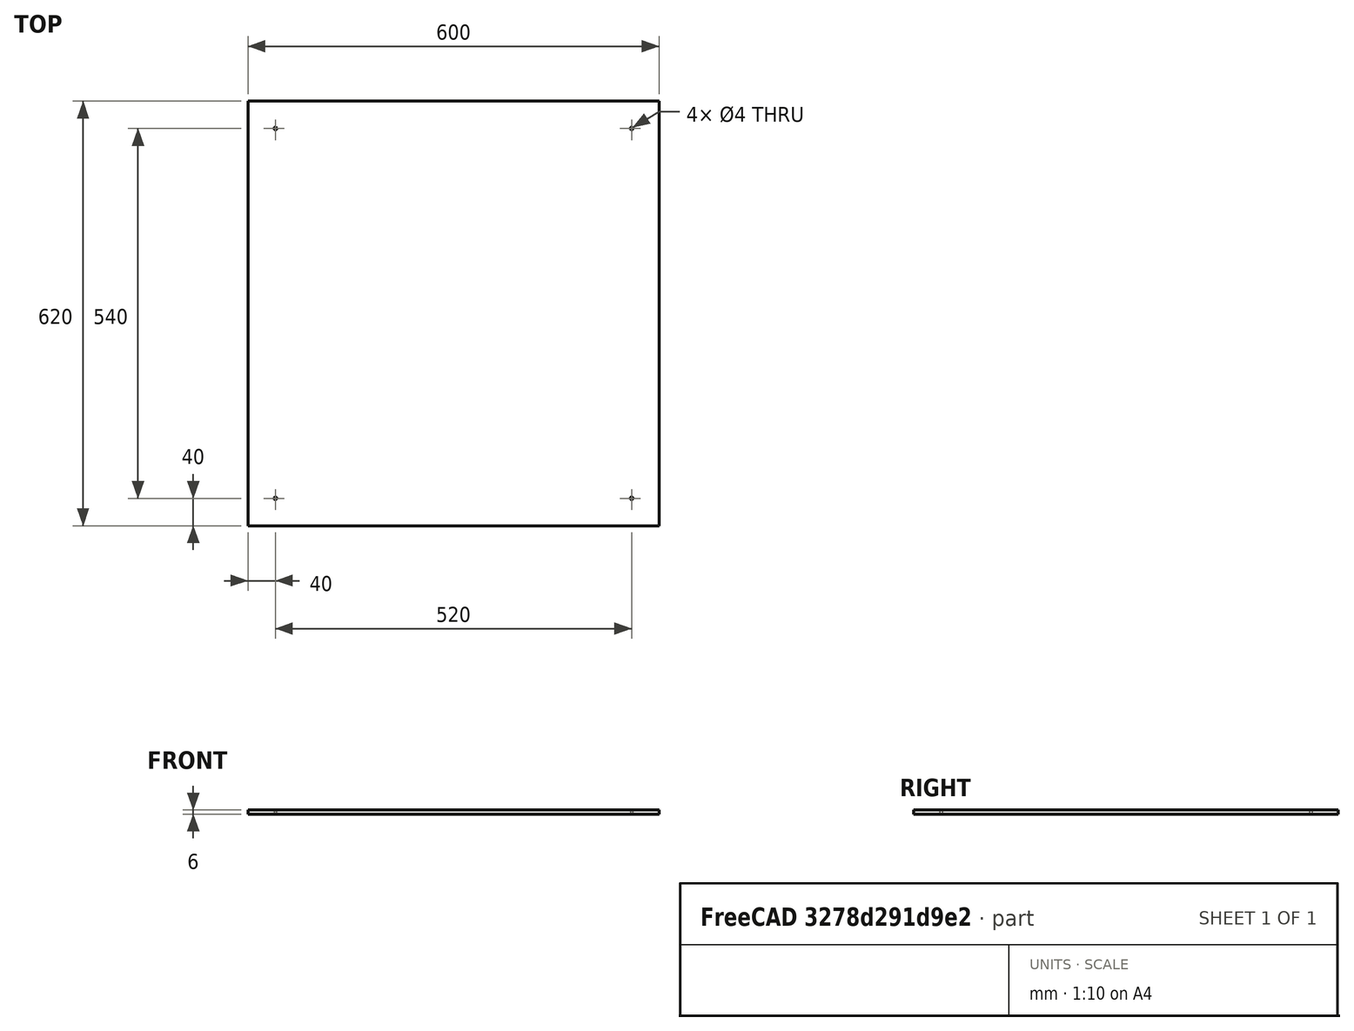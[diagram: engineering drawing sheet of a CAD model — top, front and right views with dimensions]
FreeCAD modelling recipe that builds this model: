
FCSTD DOCUMENT  (FreeCAD 1.0R39319 (Git))
Label: glass
License: All rights reserved
LicenseURL: https://en.wikipedia.org/wiki/All_rights_reserved
objects: Sketcher::SketchObject×1, PartDesign::Pad×1, PartDesign::Body×1
note: 6 computed .brp shape members not serialized (recipe doc carries the construction recipe); baked Part::Feature solids carry a one-line shape summary decoded from their .brp

FEATURE [Sketcher::SketchObject] Sketch  label="glass_s"
  ArcFitTolerance = 1e-06
  AttachmentSupport = -> [XY_Plane]
  FullyConstrained = true
  MakeInternals = false
  MapMode = 5
  sketch-geometry (16):
    g0: LineSegment StartX=0 StartY=0 StartZ=0 EndX=600 EndY=0 EndZ=0
    g1: LineSegment StartX=600 StartY=0 StartZ=0 EndX=600 EndY=620 EndZ=0
    g2: LineSegment StartX=600 StartY=620 StartZ=0 EndX=0 EndY=620 EndZ=0
    g3: LineSegment StartX=0 StartY=620 StartZ=0 EndX=0 EndY=0 EndZ=0
    g4: Circle CenterX=40 CenterY=580 CenterZ=0 NormalX=0 NormalY=0 NormalZ=1 AngleXU=0 Radius=2
    g5: Circle CenterX=560 CenterY=580 CenterZ=0 NormalX=0 NormalY=0 NormalZ=1 AngleXU=0 Radius=2
    g6: Circle CenterX=560 CenterY=40 CenterZ=0 NormalX=0 NormalY=0 NormalZ=1 AngleXU=0 Radius=2
    g7: Circle CenterX=40 CenterY=40 CenterZ=0 NormalX=0 NormalY=0 NormalZ=1 AngleXU=0 Radius=2
    g8: LineSegment [constr] StartX=40 StartY=580 StartZ=0 EndX=40 EndY=40 EndZ=0
    g9: LineSegment [constr] StartX=40 StartY=40 StartZ=0 EndX=560 EndY=40 EndZ=0
    g10: LineSegment [constr] StartX=560 StartY=40 StartZ=0 EndX=560 EndY=580 EndZ=0
    g11: LineSegment [constr] StartX=560 StartY=580 StartZ=0 EndX=40 EndY=580 EndZ=0
    g12: LineSegment [constr] StartX=560 StartY=580 StartZ=0 EndX=560 EndY=620 EndZ=0
    g13: LineSegment [constr] StartX=560 StartY=580 StartZ=0 EndX=600 EndY=580 EndZ=0
    g14: LineSegment [constr] StartX=40 StartY=40 StartZ=0 EndX=40 EndY=0 EndZ=0
    g15: LineSegment [constr] StartX=40 StartY=40 StartZ=0 EndX=0 EndY=40 EndZ=0
  constraints (43):
    c: Coincident(g0,g1)
    c: Coincident(g1,g2)
    c: Coincident(g2,g3)
    c: Coincident(g3,g0)
    c: Horizontal(g0)
    c: Horizontal(g2)
    c: Vertical(g1)
    c: Vertical(g3)
    c: Coincident(g0,g-1)
    c: DistanceY(g3,g3) = 620
    c: DistanceX(g2,g2) = 600
    c: Coincident(g8,g9)
    c: Coincident(g9,g10)
    c: Coincident(g10,g11)
    c: Coincident(g11,g8)
    c: Vertical(g8)
    c: Vertical(g10)
    c: Horizontal(g9)
    c: Horizontal(g11)
    c: Coincident(g8,g4)
    c: Coincident(g9,g6)
    c: Coincident(g7,g8)
    c: Coincident(g10,g5)
    c: Diameter(g4) = 4
    c: Equal(g4,g7)
    c: Equal(g7,g6)
    c: Equal(g6,g5)
    c: DistanceX(g0,g7) = 40
    c: Coincident(g12,g5)
    c: PointOnObject(g12,g2)
    c: Vertical(g12)
    c: PointOnObject(g13,g1)
    c: Horizontal(g13)
    c: Coincident(g13,g5)
    c: Coincident(g14,g7)
    c: PointOnObject(g14,g0)
    c: Vertical(g14)
    c: Coincident(g15,g7)
    c: PointOnObject(g15,g3)
    c: Horizontal(g15)
    c: Equal(g14,g15)
    c: Equal(g15,g13)
    c: Equal(g13,g12)
FEATURE [PartDesign::Pad] Pad
  Direction = (0,0,1)
  Length = 6
  Length2 = 10
  Profile = -> Sketch
  ReferenceAxis = -> Sketch [N_Axis]
  Refine = true
  Suppressed = false
  Type = 0
FEATURE [PartDesign::Body] Body
  AllowCompound = false
  Group = -> [Sketch,Pad]
  Origin = -> Origin
  Tip = -> Pad
